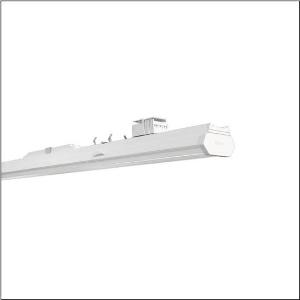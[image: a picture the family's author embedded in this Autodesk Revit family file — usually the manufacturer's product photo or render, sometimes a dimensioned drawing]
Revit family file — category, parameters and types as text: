
# Revit family: licross_r__21_protected_mo_52td1bdn4axg_daa2
name_source: partatom
category: Lighting Fixtures
units: mm (PartAtom-declared; Revit-internal decimal feet)

## family parameters
Cut with Voids When Loaded = No
Host = Face
Light Source = No
Part Type = Normal
Room Calculation Point = No
Round Connector Dimension = Use Diameter
Shared = No

## types (1)
- --- (1 x LED, 10050 lm, 62 W, 4000K)
    Apparent Load = 62 VA
    CIE Flux Codes = 54 82 95 97 100
    Color Rendering = 80
    Color Temperature = 4000K
    Default Elevation = 1800 mm
    Description = Licross® 21 Protected MO, luminaire insert, of sheet steel, galvanised, coil coated, white, length: 1.500mm, width: 90mm, height: 103mm, LED rated luminous flux: 10.060lm, light colour: 840, control gear: DALI 2, with plug, 5-pole, with phase selection, mains connection: 220..240V, AC, 50/60Hz, rated input power: 62W, halogen-free wiring, primary optical cover: cover, of PMMA, light emission: direct distribution, primary light characteristic: symmetric, protection rating (complete): IP54, insulation class (complete): insulation class I (protective earthing), certification: CE, ENEC, VDE, UKCA, protection symbol: D if used in an environment with non-conductive dust loads with corresponding accessories, impact resistance: IK06, permissible ambient temperature for indoor applications: -25..+35°C, corresponds to IFS (International Featured Standards) requirements for safety and quality in the food industry, reducing of maximum allowable ambient temperature of 5°C with ceiling mounting, LABS conformity tested according to VDMA 24364:2018-05, packaging unit: 1 piece
    Height = 92 mm
    Lamp = 1 x LED
    Lamp Light Flux = 10050 lm
    Lamp Power = 62 W
    Lamp count = 1
    Length = 1500 mm
    Luminous efficacy = 162 lm/W
    Manufacturer = Siteco
    ModVariant = No
    Model = 52TD1BDN4AXG
    Mounting Place = Ceiling
    Mounting Type = Pendant
    Number of Poles = 1
    OnlyDefault = Yes
    Power Factor = 1
    Product Name = Licross® 21 Protected MO
    Product group = luminaire insert
    ProductGroupID = 901
    Protection Class = Protection class I
    Protection Degree = IP 54
    RLX_Detail_Level = 1
    RLX_Emergency_Light_Flux = 0 lm
    RLX_Emergency_Type = 0
    RLX_Emergency_Type_DB = No
    RlxData = <blob elided: 24349 chars, md5=4e869d71>
    Socket = socket
    Standby Power = 0 W
    System Light Flux = 10050 lm
    System Power = 62 W
    Type Comments = factory setting: luminous flux: 100 % | dim-lin: 254 | 418 mA
    Type Image = l_1256148.jpg
    URL = http://relux.com
    VarID = @adj_060665
    Voltage = 0 V
    Weight = 0.00 kg
    Width = 88 mm

## geometry (parser evidence)
native form markers: Blend x4, Sweep x10
no freeform markers — native parametric forms only
